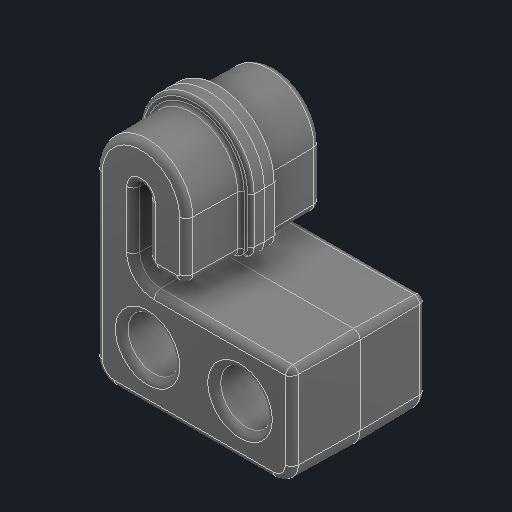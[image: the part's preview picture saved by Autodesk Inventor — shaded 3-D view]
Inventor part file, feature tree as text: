
AUTODESK INVENTOR PART (.ipt)
format: ipt  version: 2024 (Build 280153000, 153)  size: 370,688 bytes
history: native  units: in
note: dims shown in document units (in); Inventor stores cm internally (conversion verified against a paired STEP export)
features: fillet x1
ambient origin geometry x8: Origin, YZ Plane, XZ Plane, XY Plane, X Axis, Y Axis, Z Axis, Center Point
bodies: Solid1 (feature_tree)
feature tree (1):
  fillet  "Fillet6"  [1 undecoded]
note: 1 required parameter value undecoded (feature->parameter linkage not recoverable at this tier; creation-order binding heuristic only, values carry confidence <= 0.55)
